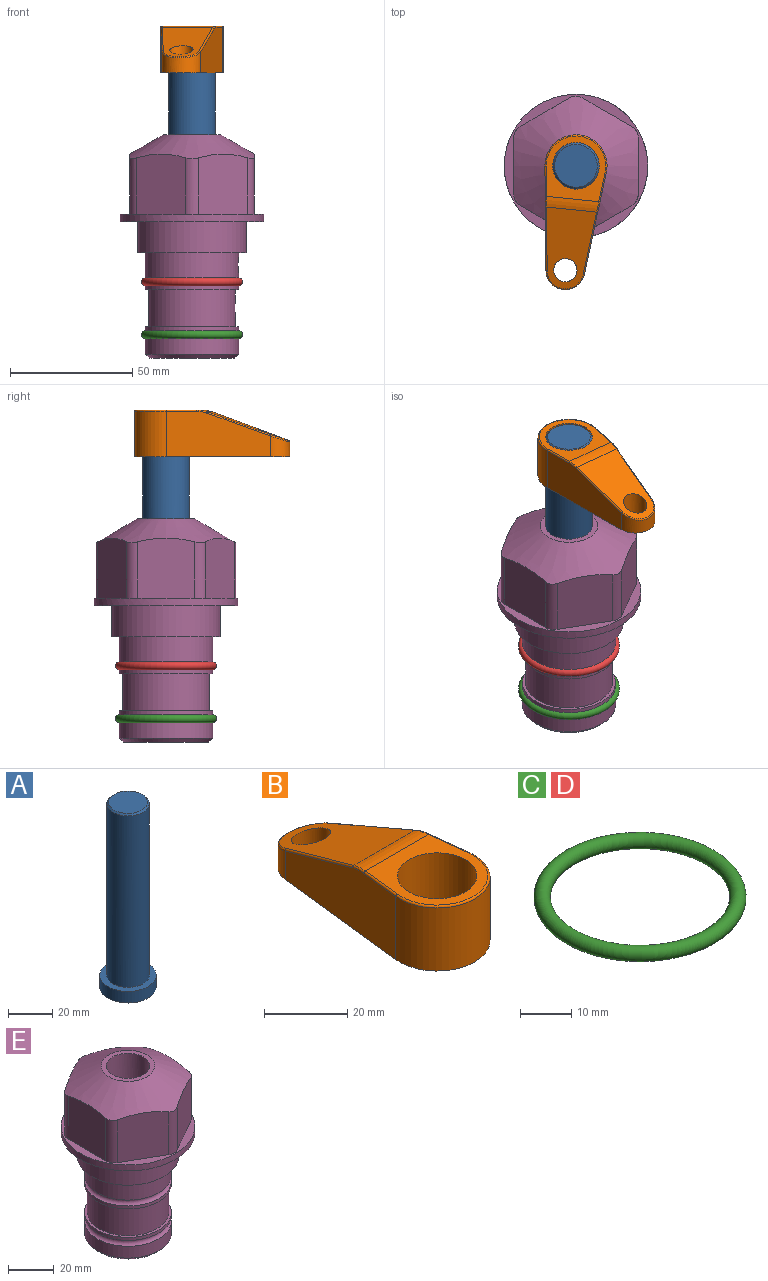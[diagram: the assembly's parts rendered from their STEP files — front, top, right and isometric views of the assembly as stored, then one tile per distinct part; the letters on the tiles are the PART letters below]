
ASSEMBLY  parts=5 mates=3
PART A: 6 faces, bbox 25.4x25.4x101.6 mm
  f0: plane 17.46x17.46mm, normal (0,0,1), area 239.5mm2, adj f5
  f1: plane 25.4x25.4mm, normal (0,0,-1), area 506.7mm2, adj f2
  f2: cylinder r=12.7mm len=25.4mm, axis (0,0,1), area 506.7mm2, adj f1,f3
  f3: plane 25.4x25.4mm, normal (0,0,1), area 221.7mm2, adj f2,f4
  f4: cylinder r=9.53mm len=94.46mm, axis (0,0,1), area 5653mm2, adj f3,f5
  f5: cone r=8.73mm half-angle=45deg, axis (0,0,-1), area 64.4mm2, adj f0,f4
PART B: 44 faces, bbox 27.5x64.5x19.1 mm
  f0: plane 2.3x0.95mm, normal (0,0,-1), area 1mm2, adj f25,f30,f34
  f1: plane 63.5x25.4mm, normal (0,0,-1), area 561.7mm2, adj f2,f3,f4,f5,f6,f7,f19,f20
  f2: cylinder r=12.7mm len=25.4mm, axis (0,0,-1), area 792.2mm2, adj f1,f3,f5,f13
  f3: plane 42.33x18.54mm, normal (0.99,0.11,0), area 647mm2, adj f1,f2,f4,f11,f12,f14
  f4: cylinder r=7.94mm len=15.78mm, axis (0,0,-1), area 158.6mm2, adj f1,f3,f5,f16
  f5: plane 42.33x18.54mm, normal (-0.99,0.11,0), area 647mm2, adj f1,f2,f4,f15,f17,f18
  f6: cylinder r=9.53mm len=19.05mm, axis (0,0,-1), area 1140.1mm2, adj f1,f8
  f7: cylinder r=4.76mm len=10.98mm, axis (0,0,-1), area 276.1mm2, adj f1,f9
  f8: plane 25.83x24.38mm, normal (0,0,1), area 262.2mm2, adj f6,f10,f11,f13,f15
  f9: plane 32.49x20.55mm, normal (0,0.34,0.94), area 489.9mm2, adj f7,f10,f14,f16,f18
  f10: cylinder r=12.7mm len=21.49mm, axis (-1,0,0), area 93.2mm2, adj f8,f9,f12,f17
  f11: cylinder r=0.51mm len=12.34mm, axis (0.11,-0.99,0), area 9.9mm2, adj f3,f8,f12,f13
  f12: bspline ~7.62x1.64mm, area 3.5mm2, adj f3,f10,f11,f14
  f13: torus R=12.19mm, axis (0,0,1), area 33.6mm2, adj f2,f8,f11,f15
  f14: cylinder r=0.51mm len=26.01mm, axis (0.1,-0.93,0.34), area 21.6mm2, adj f3,f9,f12,f16
  f15: cylinder r=0.51mm len=12.34mm, axis (0.11,0.99,0), area 9.9mm2, adj f5,f8,f13,f17
  f16: bspline ~15.78x7.05mm, area 15.7mm2, adj f4,f9,f14,f18
  f17: bspline ~7.62x1.64mm, area 3.5mm2, adj f5,f10,f15,f18
  f18: cylinder r=0.51mm len=26.01mm, axis (0.1,0.93,-0.34), area 21.6mm2, adj f5,f9,f16,f17
  f19: plane 21.6x14.29mm, normal (-0.99,-0.11,0), area 242.6mm2, adj f1,f26,f28,f34,f36,f38
  f20: plane 21.6x14.29mm, normal (0.99,-0.11,0), area 242.6mm2, adj f1,f27,f29,f37,f39,f41
  f21: cylinder r=12.7mm len=14.29mm, axis (0,0,-1), area 173.2mm2, adj f1,f26,f27,f30,f31,f33
  f22: cylinder r=7.94mm len=7.63mm, axis (0,0,-1), area 53.8mm2, adj f1,f28,f29,f42
  f23: plane 2.3x0.95mm, normal (0,0,-1), area 1mm2, adj f25,f33,f37
  f24: plane 17.94x12.32mm, normal (0,-0.34,-0.94), area 191.2mm2, adj f25,f38,f41,f42
  f25: cylinder r=9.53mm len=12.93mm, axis (-1,0,0), area 37.5mm2, adj f0,f23,f24,f31,f36,f39
  f26: cylinder r=1.59mm len=14.29mm, axis (0,0,-1), area 49mm2, adj f1,f19,f21,f32
  f27: cylinder r=1.59mm len=14.29mm, axis (0,0,-1), area 49mm2, adj f1,f20,f21,f35
  f28: cylinder r=1.59mm len=7.28mm, axis (0,0,-1), area 22.1mm2, adj f1,f19,f22,f40
  f29: cylinder r=1.59mm len=7.28mm, axis (0,0,-1), area 22.1mm2, adj f1,f20,f22,f43
  f30: torus R=14.29mm, axis (0,0,1), area 5.8mm2, adj f0,f21,f31,f32
  f31: bspline ~11.06x2.73mm, area 20.8mm2, adj f21,f25,f30,f33
  f32: sphere r=1.59mm, area 5.4mm2, adj f26,f30,f34
  f33: torus R=14.29mm, axis (0,0,1), area 5.8mm2, adj f21,f23,f31,f35
  f34: cylinder r=1.59mm len=1.68mm, axis (-0.11,0.99,0), area 2.4mm2, adj f0,f19,f32,f36
  f35: sphere r=1.59mm, area 5.4mm2, adj f27,f33,f37
  f36: bspline ~5.82x2.33mm, area 7.7mm2, adj f19,f25,f34,f38
  f37: cylinder r=1.59mm len=1.68mm, axis (0.11,0.99,0), area 2.4mm2, adj f20,f23,f35,f39
  f38: cylinder r=1.59mm len=18.33mm, axis (0.1,-0.93,0.34), area 46.7mm2, adj f19,f24,f36,f40
  f39: bspline ~5.82x2.33mm, area 7.7mm2, adj f20,f25,f37,f41
  f40: sphere r=1.59mm, area 3.6mm2, adj f28,f38,f42
  f41: cylinder r=1.59mm len=18.33mm, axis (0.1,0.93,-0.34), area 46.7mm2, adj f20,f24,f39,f43
  f42: bspline ~8.31x1.84mm, area 15.3mm2, adj f22,f24,f40,f43
  f43: sphere r=1.59mm, area 3.6mm2, adj f29,f41,f42
PART C: 1 faces, bbox 44.7x44.7x3.2 mm
  f0: torus R=19.05mm, axis (0,0,1), area 1193.9mm2
PART D: same geometry as C
PART E: 36 faces, bbox 58.7x58.7x91.2 mm
  f0: cylinder r=17.78mm len=35.56mm, axis (0,0,1), area 1670.8mm2, adj f23,f24,f31
  f1: cylinder r=19.05mm len=38.1mm, axis (0,0,1), area 1191.9mm2, adj f26,f27,f30
  f2: plane 58.66x58.66mm, normal (0,0,-1), area 1150.6mm2, adj f3,f28
  f3: cylinder r=29.33mm len=58.66mm, axis (0,0,-1), area 585.1mm2, adj f2,f4
  f4: plane 58.66x58.66mm, normal (0,0,1), area 475.9mm2, adj f3,f5,f6,f7,f8,f9,f10,f11
  f5: plane 24.5x20.32mm, normal (-0.5,0.87,0), area 562.8mm2, adj f4,f15,f16,f17
  f6: plane 24.5x20.32mm, normal (0.5,0.87,0), area 562.8mm2, adj f4,f14,f15,f17
  f7: plane 24.5x23.48mm, normal (1,0,0), area 562.8mm2, adj f4,f13,f14,f17
  f8: plane 24.5x20.32mm, normal (0.5,-0.87,0), area 562.8mm2, adj f4,f12,f13,f17
  f9: plane 24.5x20.32mm, normal (-0.5,-0.87,0), area 562.8mm2, adj f4,f11,f12,f17
  f10: plane 24.5x23.48mm, normal (-1,0,0), area 562.8mm2, adj f4,f11,f16,f17
  f11: cylinder r=5.08mm len=23.01mm, axis (0,0,-1), area 121.2mm2, adj f4,f9,f10,f17
  f12: cylinder r=5.08mm len=23.01mm, axis (0,0,-1), area 121.2mm2, adj f4,f8,f9,f17
  f13: cylinder r=5.08mm len=23.01mm, axis (0,0,-1), area 121.2mm2, adj f4,f7,f8,f17
  f14: cylinder r=5.08mm len=23.01mm, axis (0,0,-1), area 121.2mm2, adj f4,f6,f7,f17
  f15: cylinder r=5.08mm len=23.01mm, axis (0,0,-1), area 121.2mm2, adj f4,f5,f6,f17
  f16: cylinder r=5.08mm len=23.01mm, axis (0,0,-1), area 121.2mm2, adj f4,f5,f10,f17
  f17: cone r=11.73mm half-angle=60deg, axis (0,0,-1), area 2071.8mm2, adj f5,f6,f7,f8,f9,f10,f11,f12
  f18: plane 23.46x23.46mm, normal (0,0,1), area 147.4mm2, adj f17,f35
  f19: plane 34.93x34.93mm, normal (0,0,-1), area 958mm2, adj f29
  f20: cylinder r=19.05mm len=38.1mm, axis (0,0,1), area 760.1mm2, adj f21,f29
  f21: torus R=19.05mm, axis (0,0,1), area 565.3mm2, adj f20,f22
  f22: cylinder r=19.05mm len=38.1mm, axis (0,0,1), area 190mm2, adj f21,f23
  f23: plane 38.1x38.1mm, normal (0,0,1), area 146.9mm2, adj f0,f22
  f24: plane 38.1x38.1mm, normal (0,0,-1), area 146.9mm2, adj f0,f25
  f25: cylinder r=19.05mm len=38.1mm, axis (0,0,1), area 190mm2, adj f24,f26
  f26: torus R=19.05mm, axis (0,0,1), area 565.3mm2, adj f1,f25
  f27: plane 44.45x44.45mm, normal (0,0,-1), area 411.7mm2, adj f1,f28
  f28: cylinder r=22.23mm len=44.45mm, axis (0,0,1), area 1773.5mm2, adj f2,f27
  f29: cone r=19.05mm half-angle=45deg, axis (0,0,1), area 257.5mm2, adj f19,f20
  f30: cylinder r=3.17mm len=6.75mm, axis (-1,0,0), area 128mm2, adj f1,f33
  f31: cylinder r=3.17mm len=6.35mm, axis (-1,0,0), area 102.5mm2, adj f0,f33
  f32: plane 25.4x25.4mm, normal (0,0,1), area 506.7mm2, adj f33
  f33: cylinder r=12.7mm len=66.42mm, axis (0,0,-1), area 5236.2mm2, adj f30,f31,f32,f34
  f34: cone r=9.53mm half-angle=30deg, axis (0,0,-1), area 443.4mm2, adj f33,f35
  f35: cylinder r=9.53mm len=19.05mm, axis (0,0,-1), area 849mm2, adj f18,f34
PLACE A rot(axis=(0,0,-1),95.8deg) t=(0,0,6.38)mm
PLACE B rot(axis=(0,0,1),174.2deg) t=(0,0,60.99)mm
PLACE C t=(0,0,-21.59)mm
PLACE D at identity
PLACE E at identity fixed
MATE fastened C.f0 <-> E.f0  axis (0,0,1) through (0,0,-46.1)mm
MATE cylindrical A.f2 <-> E.f0  axis (0,0,1) through (0,0,32.01)mm
MATE fastened B.f2 <-> A.f2  axis (0,0,1) through (0,0,80.04)mm
